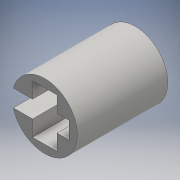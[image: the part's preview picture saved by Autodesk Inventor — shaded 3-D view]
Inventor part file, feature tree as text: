
AUTODESK INVENTOR PART (.ipt)
format: ipt  version: 2016 (Build 200138000, 138)  size: 137,216 bytes
history: native  units: mm
features: other x4, extrude x3, hole x1, sketch x1
ambient origin geometry x8: Origin, YZ Plane, XZ Plane, XY Plane, X Axis, Y Axis, Z Axis, Center Point
bodies: Solid1 (feature_tree)
feature tree (9):
  other  "zero_sketch.ipt"
  extrude  "Extrusion1"  Depth=3.85mm TaperAngle=0.0deg
  extrude  "Extrusion2"  Depth=10.0mm
  extrude  "Extrusion3"  Depth=1.05mm TaperAngle=0.0deg
  hole  "Hole1"  [1 undecoded]
  other  "base+body"
  other  "base+body_1"
  other  "base+body_2"
  sketch  "Sketch5"  dims[d0=10.0mm d1=3.85mm d2=0.0mm d3=10.0mm d4=7.85mm d5=0.0mm d6=10.0mm d7=1.7mm d8=0.0mm d10=0.6mm d11=6.0mm d12=2.5mm d13=1.05mm d14=90.0deg d15=8.0mm d16=20.594885mm]
note: 1 required parameter value undecoded (feature->parameter linkage not recoverable at this tier; creation-order binding heuristic only, values carry confidence <= 0.55)
